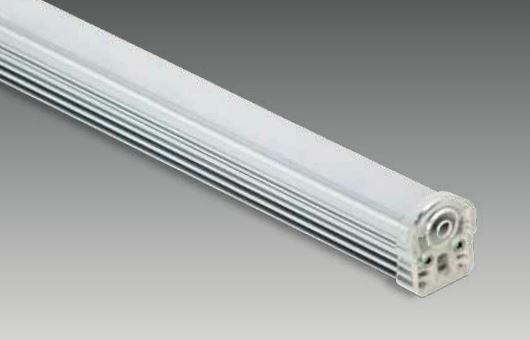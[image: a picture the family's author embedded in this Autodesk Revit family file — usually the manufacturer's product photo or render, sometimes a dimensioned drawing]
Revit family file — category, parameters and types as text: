
# Revit family: SD 1245 CVI
name_source: partatom
category: Lighting Fixtures
revit_build: Autodesk Revit 2017 (Build: 20160225_1515(x64)
units: mm (PartAtom-declared; Revit-internal decimal feet)

## family parameters
Cut with Voids When Loaded = No
Host = Face
Light Source = Yes
Part Type = Normal
Room Calculation Point = No
Round Connector Dimension = Use Diameter
Shared = No

## types (2) — shared parameters
Apparent Load = 20 VA
Color Filter = 16777215
Default Elevation = 1219 mm
Dimming Lamp Color Temperature Shift = <None>
Emit Shape Visible in Rendering = Yes
Emit from Rectangle Length = 15 mm  [stored 0.0492126 ft]
Emit from Rectangle Width = 1240 mm  [stored 4.06824 ft]
Light Source Symbol Size = 610 mm
Manufacturer = ARLIGHT
Type Image = SD 1245 CVI.JPG
Wattage Comments = 20

## type names (no varying parameters)
- SDCVI.1245.20.30
- SDCVI.1245.20.40

note: [stored X ft] marks values corroborated as IEEE doubles in the binary element streams (Revit-internal decimal feet)

## geometry (parser evidence)
native form markers: Sweep x2
no freeform markers — native parametric forms only
